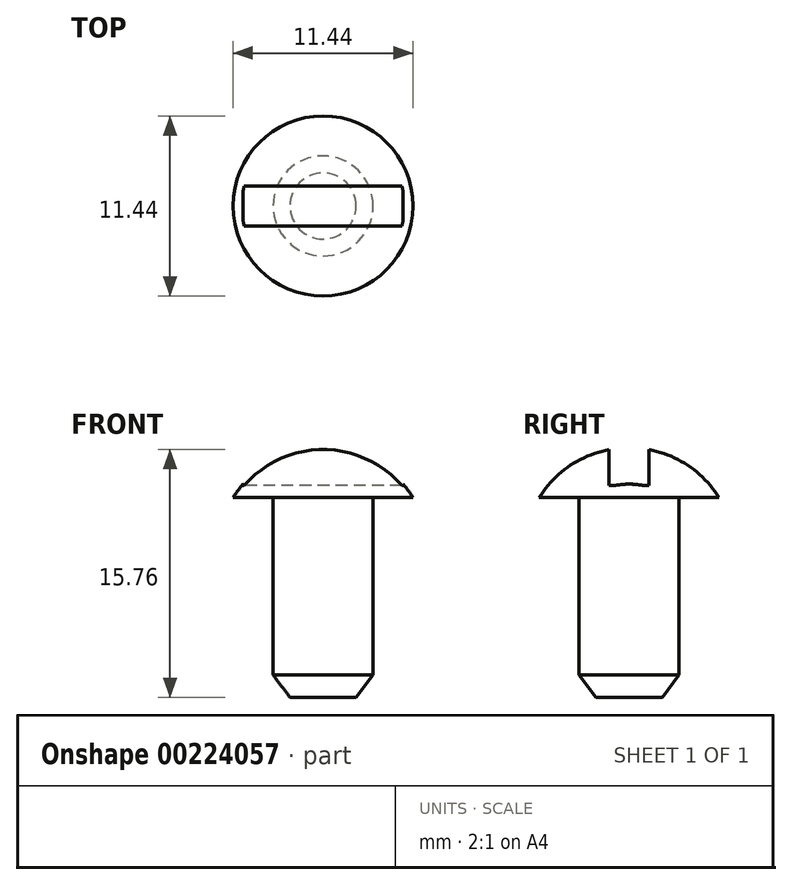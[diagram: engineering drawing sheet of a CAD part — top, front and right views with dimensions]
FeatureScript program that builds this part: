
annotation { "Feature Type Name" : "Feature", "Feature Type Description" : "" }
export const myFeature = defineFeature(function(context is Context, id is Id, definition is map)
    precondition{}
    {
        {
            var Q0;
            Q0=qCreatedBy(makeId("Front.planeOp"),FACE);
            var sketch = newSketch(context, id + "F0", { "sketchPlane" : qUnion([Q0])});
            skLineSegment(sketch, "E0.bottom", {"start": v(0, 0) * mm, "end": v(2.1, 0) * mm});
            skLineSegment(sketch, "E0.left", {"start": v(0, 0) * mm, "end": v(0, 15.88) * mm});
            skLineSegment(sketch, "E0.right", {"start": v(3.18, 1.46) * mm, "end": v(3.17, 12.7) * mm});
            skLineSegment(sketch, "E1", {"start": v(3.17, 12.7) * mm, "end": v(5.12, 12.7) * mm});
            skLineSegment(sketch, "E2", {"start": v(2.1, 0) * mm, "end": v(3.18, 1.46) * mm});
            skLineSegment(sketch, "E3", {"start": v(3.17, 12.7) * mm, "end": v(5.72, 12.7) * mm});
            skArc(sketch, "E4", {"start": v(5.72, 12.7) * mm, "mid": v(3.27, 15.03) * mm, "end": v(0, 15.88) * mm});
            skPoint(sketch, "E5.orphan", {"position": v(0, 12.7) * mm});
            skSolve(sketch);
        }
        {
            var Q0;
            Q0=makeQuery(id+"F0.imprint","IMPRINT",FACE,{"disambiguationData":[TD([[makeQuery(id+"F0.imprint","IMPRINT",EDGE,{"derivedFrom":sQuery(id+"F0.wireOp",EDGE,"E0.bottom")}),1.0]])]});
            var Q1;
            Q1=sQuery(id+"F0.wireOp",EDGE,"E0.left");
            revolve(context, id + "F1", {"entities" : qUnion([Q0]), "axis" : qUnion([Q1]), "revolveType" : RevolveType.FULL});
        }
        {
            var Q0;
            Q0=qCreatedBy(makeId("Top.planeOp"),FACE);
            cPlane(context, id + "F2", {"entities" : qUnion([Q0]), "cplaneType" : CPlaneType.OFFSET, "offset" : 13.46 * mm, "width" : 152.4 * mm, "height" : 152.4 * mm});
        }
        {
            var Q0;
            Q0=qCreatedBy(id+"F2.planeOp",FACE);
            var sketch = newSketch(context, id + "F3", { "sketchPlane" : qUnion([Q0])});
            skLineSegment(sketch, "E6.bottom", {"start": v(5.08, 1.27) * mm, "end": v(-5.08, 1.27) * mm});
            skLineSegment(sketch, "E6.top", {"start": v(5.08, -1.27) * mm, "end": v(-5.08, -1.27) * mm});
            skLineSegment(sketch, "E6.left", {"start": v(5.08, 1.27) * mm, "end": v(5.08, -1.27) * mm});
            skLineSegment(sketch, "E6.right", {"start": v(-5.08, 1.27) * mm, "end": v(-5.08, -1.27) * mm});
            skPoint(sketch, "E6.middle", {"position": v(0, 0) * mm});
            skSolve(sketch);
        }
        {
            var Q0;
            Q0 = qSketchRegion(id + "F3", true);
            extrude(context, id + "F4", {"entities" : qUnion([Q0]), "operationType" : NewBodyOperationType.REMOVE, "depth" : 76.2 * mm});
        }
    });
